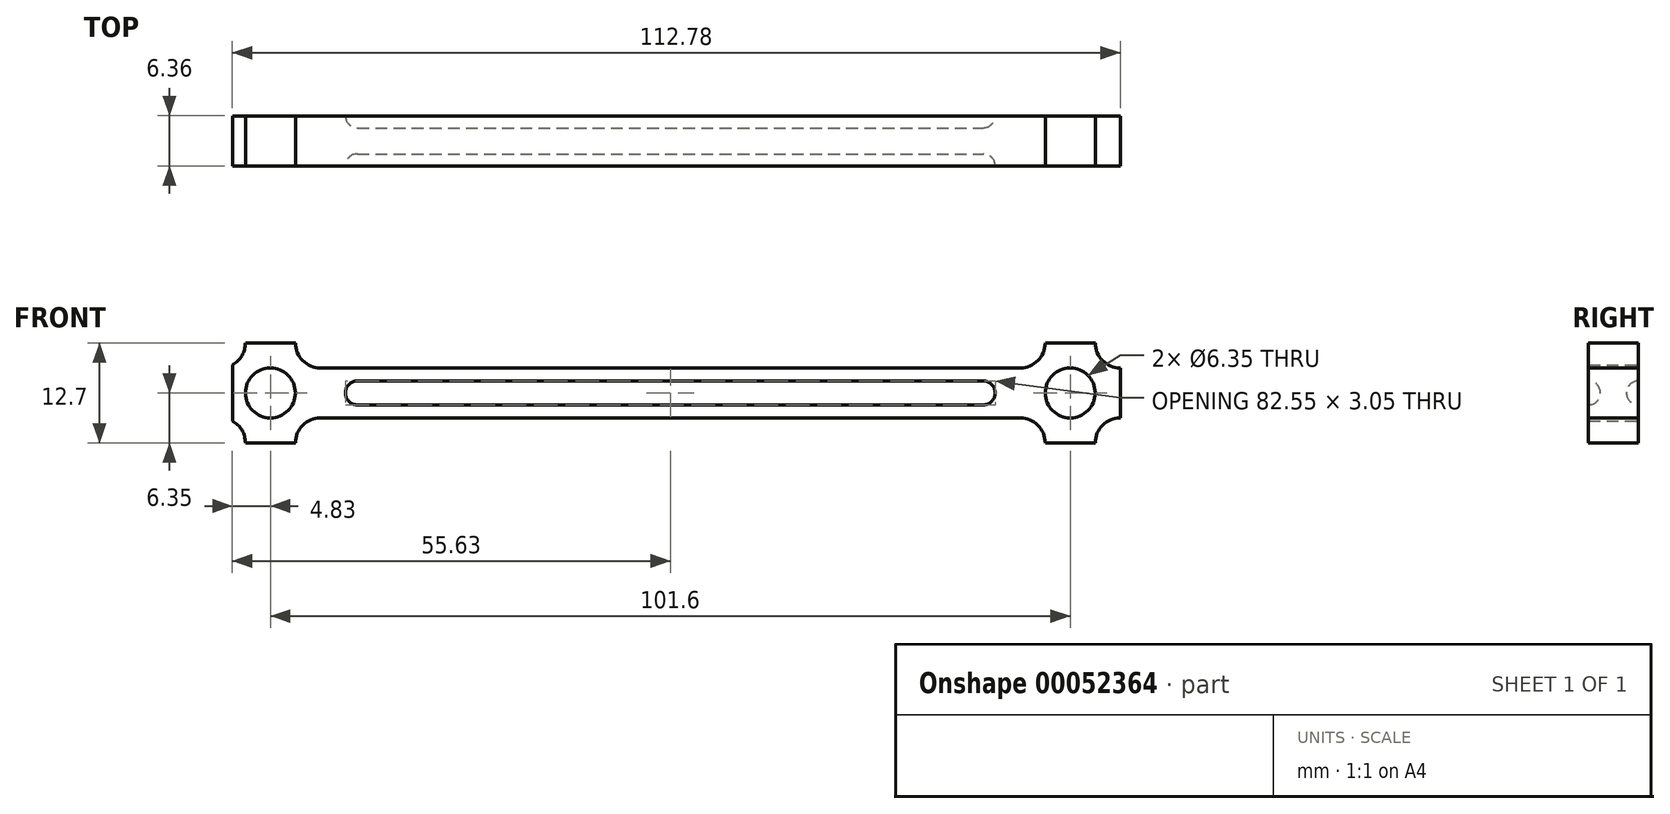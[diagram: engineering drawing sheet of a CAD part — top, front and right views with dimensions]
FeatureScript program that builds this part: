
annotation { "Feature Type Name" : "Feature", "Feature Type Description" : "" }
export const myFeature = defineFeature(function(context is Context, id is Id, definition is map)
    precondition{}
    {
        {
            var Q0;
            Q0=qCreatedBy(makeId("Front.planeOp"),FACE);
            var sketch = newSketch(context, id + "F0", { "sketchPlane" : qUnion([Q0])});
            skLineSegment(sketch, "E0", {"start": v(-44.45, 3.17) * mm, "end": v(44.45, 3.17) * mm});
            skArc(sketch, "E1", {"start": v(44.45, 3.17) * mm, "mid": v(46.7, 4.1) * mm, "end": v(47.63, 6.35) * mm});
            skLineSegment(sketch, "E2", {"start": v(47.62, 6.35) * mm, "end": v(53.98, 6.35) * mm});
            skLineSegment(sketch, "E3", {"start": v(57.15, 3.18) * mm, "end": v(57.15, -3.18) * mm});
            skLineSegment(sketch, "E4", {"start": v(53.98, -6.35) * mm, "end": v(47.62, -6.35) * mm});
            skLineSegment(sketch, "E5", {"start": v(44.45, -3.18) * mm, "end": v(-44.45, -3.18) * mm});
            skCircle(sketch, "E6", {"center": v(50.8, 0) * mm, "radius": 3.18 * mm});
            skCircle(sketch, "E7", {"center": v(-50.8, 0) * mm, "radius": 3.18 * mm});
            skPoint(sketch, "E8", {"position": v(0, 3.18) * mm});
            skPoint(sketch, "E9", {"position": v(57.15, 0) * mm});
            skArc(sketch, "E10", {"start": v(53.98, 6.35) * mm, "mid": v(54.9, 4.1) * mm, "end": v(57.15, 3.17) * mm});
            skPoint(sketch, "E11", {"position": v(50.8, 6.35) * mm});
            skPoint(sketch, "E12", {"position": v(50.8, -6.35) * mm});
            skArc(sketch, "E13", {"start": v(47.63, -6.35) * mm, "mid": v(46.7, -4.1) * mm, "end": v(44.45, -3.18) * mm});
            skArc(sketch, "E14", {"start": v(57.15, -3.17) * mm, "mid": v(54.9, -4.1) * mm, "end": v(53.98, -6.35) * mm});
            skArc(sketch, "E15", {"start": v(-47.62, 6.35) * mm, "mid": v(-46.7, 4.1) * mm, "end": v(-44.45, 3.18) * mm});
            skArc(sketch, "E16", {"start": v(-44.45, -3.18) * mm, "mid": v(-46.7, -4.1) * mm, "end": v(-47.62, -6.35) * mm});
            skLineSegment(sketch, "E17", {"start": v(-47.62, 6.35) * mm, "end": v(-53.97, 6.35) * mm});
            skLineSegment(sketch, "E18", {"start": v(-47.62, -6.35) * mm, "end": v(-53.97, -6.35) * mm});
            skArc(sketch, "E19", {"start": v(-55.63, 3.56) * mm, "mid": v(-54.42, 4.73) * mm, "end": v(-53.97, 6.35) * mm});
            skArc(sketch, "E20", {"start": v(-53.97, -6.35) * mm, "mid": v(-54.42, -4.73) * mm, "end": v(-55.63, -3.56) * mm});
            skPoint(sketch, "E21", {"position": v(-50.8, 6.35) * mm});
            skLineSegment(sketch, "E22", {"start": v(-55.63, 3.56) * mm, "end": v(-55.63, -3.56) * mm});
            skPoint(sketch, "E23.orphan", {"position": v(-57.15, 3.18) * mm});
            skPoint(sketch, "E24.orphan", {"position": v(-57.15, -3.18) * mm});
            skSolve(sketch);
        }
        {
            var Q0;
            Q0 = qSketchRegion(id + "F0", true);
            extrude(context, id + "F1", {"entities" : qUnion([Q0]), "depth" : 6.35 * mm, "symmetric" : true});
        }
        {
            var Q0;
            Q0=qCreatedBy(makeId("Right.planeOp"),FACE);
            var sketch = newSketch(context, id + "F2", { "sketchPlane" : qUnion([Q0])});
            skArc(sketch, "E25", {"start": v(3.17, 1.52) * mm, "mid": v(1.65, 0) * mm, "end": v(3.18, -1.52) * mm});
            skArc(sketch, "E26", {"start": v(-3.18, -1.52) * mm, "mid": v(-1.65, 0) * mm, "end": v(-3.18, 1.52) * mm});
            skLineSegment(sketch, "E27", {"start": v(3.18, -1.52) * mm, "end": v(3.17, 1.52) * mm});
            skLineSegment(sketch, "E28", {"start": v(-3.18, -1.52) * mm, "end": v(-3.18, 1.52) * mm});
            skSolve(sketch);
        }
        {
            var Q0;
            Q0 = qSketchRegion(id + "F2", true);
            extrude(context, id + "F3", {"entities" : qUnion([Q0]), "operationType" : NewBodyOperationType.REMOVE, "oppositeDirection" : true, "depth" : 82.55 * mm, "symmetric" : true});
        }
        {
            var Q0;
            Q0=makeQuery(id+"F3.boolean.opBoolean","COPY",EDGE,{"derivedFrom":makeQuery(id+"F3.opExtrude","CAP_EDGE",EDGE,{"disambiguationData":[OSD([sQuery(id+"F2.wireOp",EDGE,"E25")])],"isStart":true})});
            var Q1;
            Q1=makeQuery(id+"F3.boolean.opBoolean","COPY",EDGE,{"derivedFrom":makeQuery(id+"F3.opExtrude","CAP_EDGE",EDGE,{"disambiguationData":[OSD([sQuery(id+"F2.wireOp",EDGE,"E25")])],"isStart":false})});
            var Q2;
            Q2=makeQuery(id+"F3.boolean.opBoolean","COPY",EDGE,{"derivedFrom":makeQuery(id+"F3.opExtrude","CAP_EDGE",EDGE,{"disambiguationData":[OSD([sQuery(id+"F2.wireOp",EDGE,"E26")])],"isStart":false})});
            var Q3;
            Q3=makeQuery(id+"F3.boolean.opBoolean","COPY",EDGE,{"derivedFrom":makeQuery(id+"F3.opExtrude","CAP_EDGE",EDGE,{"disambiguationData":[OSD([sQuery(id+"F2.wireOp",EDGE,"E26")])],"isStart":true})});
            fillet(context, id + "F4", {"entities" : qUnion([Q0, Q1, Q2, Q3]), "radius" : 1.52 * mm, "tangentPropagation" : true, "allowEdgeOverflow" : false});
        }
    });
